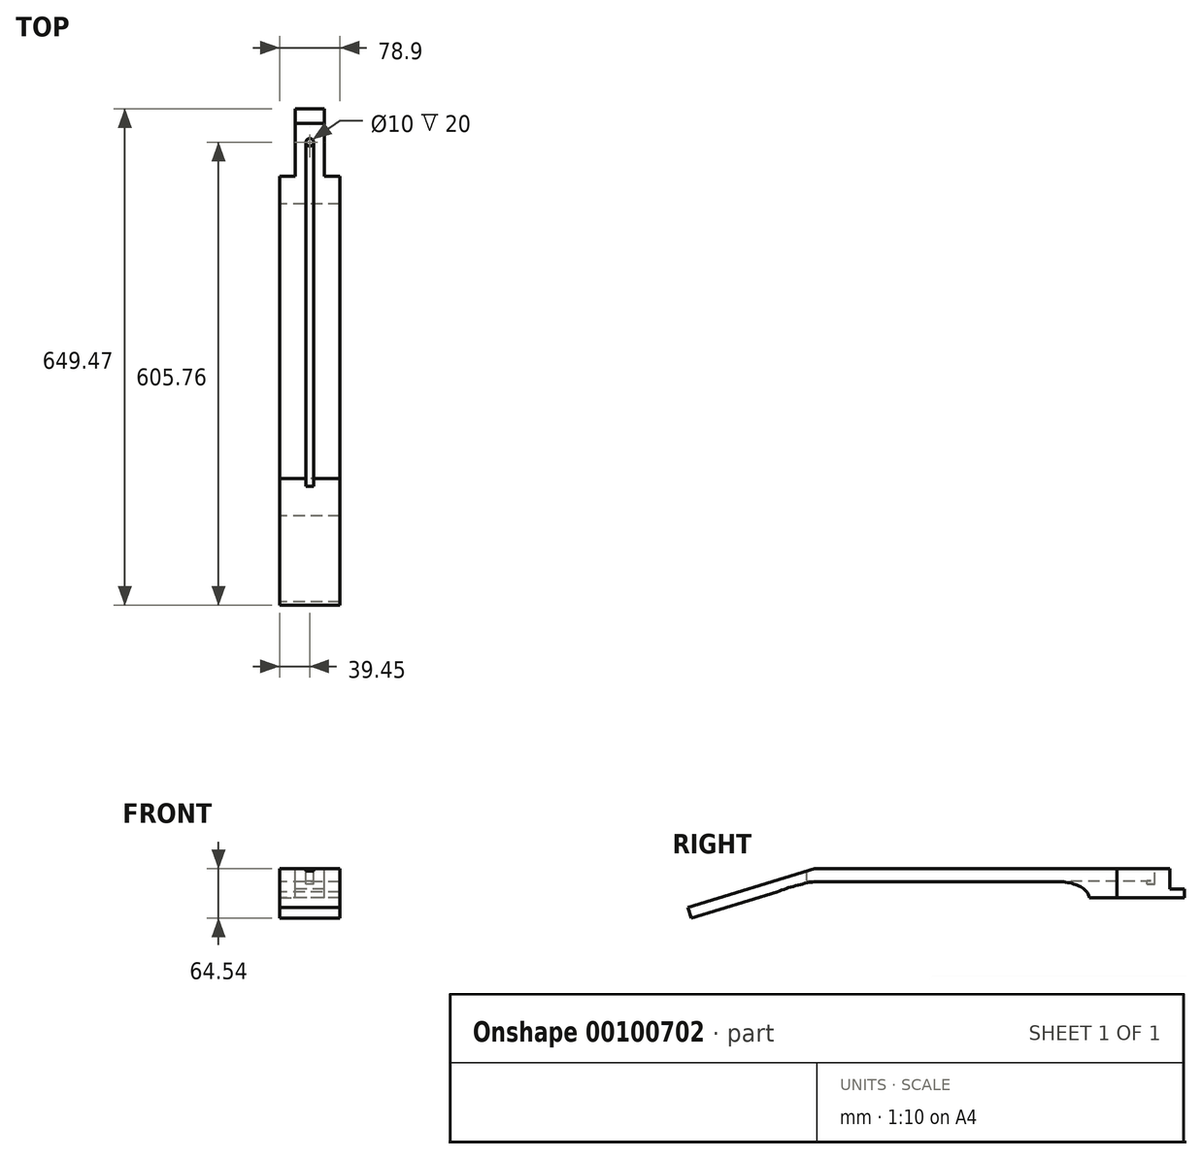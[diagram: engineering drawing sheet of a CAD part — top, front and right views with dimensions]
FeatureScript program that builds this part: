
annotation { "Feature Type Name" : "Feature", "Feature Type Description" : "" }
export const myFeature = defineFeature(function(context is Context, id is Id, definition is map)
    precondition{}
    {
        {
            var Q0;
            Q0=qCreatedBy(makeId("Right.planeOp"),FACE);
            var sketch = newSketch(context, id + "F0", { "sketchPlane" : qUnion([Q0])});
            skLineSegment(sketch, "E0", {"start": v(0, 0) * mm, "end": v(0, 11.4) * mm});
            skLineSegment(sketch, "E1", {"start": v(0, 11.4) * mm, "end": v(-18.67, 11.4) * mm});
            skLineSegment(sketch, "E2", {"start": v(-18.67, 11.4) * mm, "end": v(-18.67, 38.1) * mm});
            skLineSegment(sketch, "E3", {"start": v(-18.67, 38.1) * mm, "end": v(-483.73, 38.1) * mm});
            skLineSegment(sketch, "E4", {"start": v(-483.73, 38.1) * mm, "end": v(-483.73, -26.44) * mm, "construction": true});
            skLineSegment(sketch, "E5", {"start": v(-483.73, -26.44) * mm, "end": v(-645.23, -26.44) * mm, "construction": true});
            skLineSegment(sketch, "E6", {"start": v(0, 0) * mm, "end": v(-124.5, 0) * mm});
            skLineSegment(sketch, "E7", {"start": v(-483.73, 38.1) * mm, "end": v(-649.47, -12.57) * mm});
            skLineSegment(sketch, "E8", {"start": v(-645.23, -26.44) * mm, "end": v(-649.47, -12.57) * mm});
            skPoint(sketch, "E9.orphan", {"position": v(-608.35, 0) * mm});
            skLineSegment(sketch, "E10", {"start": v(-645.23, -26.44) * mm, "end": v(-532.73, 7.96) * mm});
            skLineSegment(sketch, "E11", {"start": v(-483.73, 5.83) * mm, "end": v(-532.73, 5.83) * mm, "construction": true});
            skLineSegment(sketch, "E12", {"start": v(-532.73, 5.83) * mm, "end": v(-532.73, 44.97) * mm, "construction": true});
            skPoint(sketch, "E13.orphan", {"position": v(-558.76, 0) * mm});
            skLineSegment(sketch, "E14", {"start": v(-483.73, 21.3) * mm, "end": v(-425.73, 21.3) * mm});
            skArc(sketch, "E15", {"start": v(-483.73, 21.3) * mm, "mid": v(-508.57, 15.88) * mm, "end": v(-532.73, 7.96) * mm});
            skLineSegment(sketch, "E16", {"start": v(-124.5, 0) * mm, "end": v(-166.5, 0) * mm, "construction": true});
            skLineSegment(sketch, "E17", {"start": v(-166.5, 0) * mm, "end": v(-166.5, 35) * mm, "construction": true});
            skLineSegment(sketch, "E18", {"start": v(-425.73, 21.3) * mm, "end": v(-166.5, 21.3) * mm});
            skEllipticalArc(sketch, "E19", {});
            const initialGuessF0  = {"E19": [-0.1665, 0, 1, 0, 0.042, 0.0213, 0, 1.5707963267948966]};
            skSetInitialGuess(sketch, initialGuessF0);
            skSolve(sketch);
        }
        {
            var Q0;
            Q0=qSketchRegion(id+"F0",true);
            extrude(context, id + "F1", {"entities" : qUnion([Q0]), "depth" : 78.9 * mm, "symmetric" : true});
        }
        {
            var Q0;
            Q0=makeQuery(id+"F1.opExtrude","SWEPT_FACE",FACE,{"disambiguationData":[OSD([sQuery(id+"F0.wireOp",EDGE,"E3")])]});
            var sketch = newSketch(context, id + "F2", { "sketchPlane" : qUnion([Q0])});
            skLineSegment(sketch, "E20", {"start": v(0, 0) * mm, "end": v(19.05, 0) * mm, "construction": true});
            skLineSegment(sketch, "E21", {"start": v(0, 0) * mm, "end": v(0, -88) * mm, "construction": true});
            skLineSegment(sketch, "E22", {"start": v(0, -88) * mm, "end": v(19.05, -88) * mm, "construction": true});
            skLineSegment(sketch, "E23.bottom", {"start": v(19.05, -88) * mm, "end": v(56.05, -88) * mm});
            skLineSegment(sketch, "E23.top", {"start": v(19.05, 19.3) * mm, "end": v(56.05, 19.3) * mm});
            skLineSegment(sketch, "E23.left", {"start": v(19.05, -88) * mm, "end": v(19.05, 19.3) * mm});
            skLineSegment(sketch, "E23.right", {"start": v(56.05, -88) * mm, "end": v(56.05, 19.3) * mm});
            skLineSegment(sketch, "E24.MirrorCS", {"start": v(-19.05, -88) * mm, "end": v(-19.05, 19.3) * mm});
            skLineSegment(sketch, "E25.MirrorCS", {"start": v(-19.05, 19.3) * mm, "end": v(-56.05, 19.3) * mm});
            skLineSegment(sketch, "E26.MirrorCS", {"start": v(-56.05, -88) * mm, "end": v(-56.05, 19.3) * mm});
            skLineSegment(sketch, "E27.MirrorCS", {"start": v(-19.05, -88) * mm, "end": v(-56.05, -88) * mm});
            skSolve(sketch);
        }
        {
            var Q0;
            Q0=qSketchRegion(id+"F2",true);
            extrude(context, id + "F10", {"entities" : qUnion([Q0]), "operationType" : NewBodyOperationType.REMOVE, "endBound" : BoundingType.THROUGH_ALL, "oppositeDirection" : true, "depth" : 25 * mm});
        }
        {
            var Q0;
            Q0=makeQuery(id+"F1.opExtrude","SWEPT_FACE",FACE,{"disambiguationData":[OSD([sQuery(id+"F0.wireOp",EDGE,"E3")])]});
            var sketch = newSketch(context, id + "F3", { "sketchPlane" : qUnion([Q0])});
            skLineSegment(sketch, "E28", {"start": v(0, -18.67) * mm, "end": v(0, -38.71) * mm, "construction": true});
            skLineSegment(sketch, "E29", {"start": v(0, -38.71) * mm, "end": v(0, -48.7) * mm, "construction": true});
            skPoint(sketch, "E30", {"position": v(0, -43.71) * mm});
            skCircle(sketch, "E31", {"center": v(0, -43.71) * mm, "radius": 5 * mm});
            skSolve(sketch);
        }
        {
            var Q0;
            Q0=qSketchRegion(id+"F3",true);
            extrude(context, id + "F4", {"entities" : qUnion([Q0]), "operationType" : NewBodyOperationType.REMOVE, "oppositeDirection" : true, "depth" : 20 * mm});
        }
        {
            var Q0;
            Q0=qCreatedBy(makeId("Front.planeOp"),FACE);
            var Q1;
            Q1=sQuery(id+"F3.wireOp",VERTEX,"E30");
            cPlane(context, id + "F5", {"entities" : qUnion([Q0, Q1]), "cplaneType" : CPlaneType.PLANE_POINT, "offset" : 25 * mm, "width" : 150 * mm, "height" : 150 * mm});
        }
        {
            var Q0;
            Q0=qCreatedBy(id+"F5.planeOp",FACE);
            var sketch = newSketch(context, id + "F6", { "sketchPlane" : qUnion([Q0])});
            skLineSegment(sketch, "E32.bottom", {"start": v(-5, 22.55) * mm, "end": v(5, 22.55) * mm});
            skLineSegment(sketch, "E32.top", {"start": v(-5, 54.3) * mm, "end": v(5, 54.3) * mm});
            skLineSegment(sketch, "E32.left", {"start": v(-5, 22.55) * mm, "end": v(-5, 54.3) * mm});
            skLineSegment(sketch, "E32.right", {"start": v(5, 22.55) * mm, "end": v(5, 54.3) * mm});
            skPoint(sketch, "E32.middle", {"position": v(0, 38.43) * mm});
            skSolve(sketch);
        }
        {
            var Q0;
            Q0=qSketchRegion(id+"F6",true);
            extrude(context, id + "F7", {"entities" : qUnion([Q0]), "operationType" : NewBodyOperationType.REMOVE, "depth" : 450 * mm});
        }
    });
